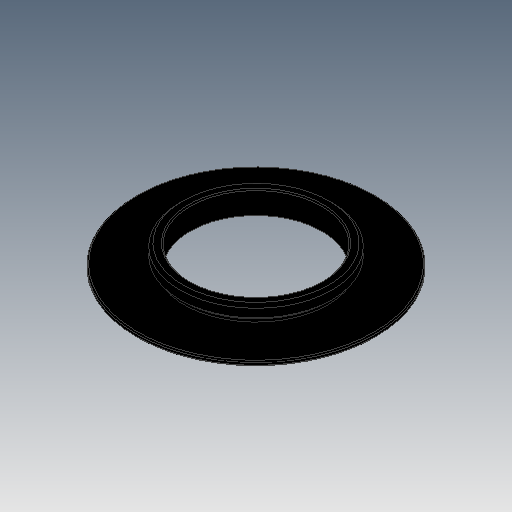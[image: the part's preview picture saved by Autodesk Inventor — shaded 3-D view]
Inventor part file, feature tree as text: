
AUTODESK INVENTOR PART (.ipt)
format: ipt  version: 2019 (Build 230136000, 136)  size: 124,416 bytes
history: native  units: mm
features: chamfer x1
ambient origin geometry x8: Origin, YZ Plane, XZ Plane, XY Plane, X Axis, Y Axis, Z Axis, Center Point
bodies: Solid1 (feature_tree)
feature tree (1):
  chamfer  "Chamfer4"  [1 undecoded]
note: 1 required parameter value undecoded (feature->parameter linkage not recoverable at this tier; creation-order binding heuristic only, values carry confidence <= 0.55)
